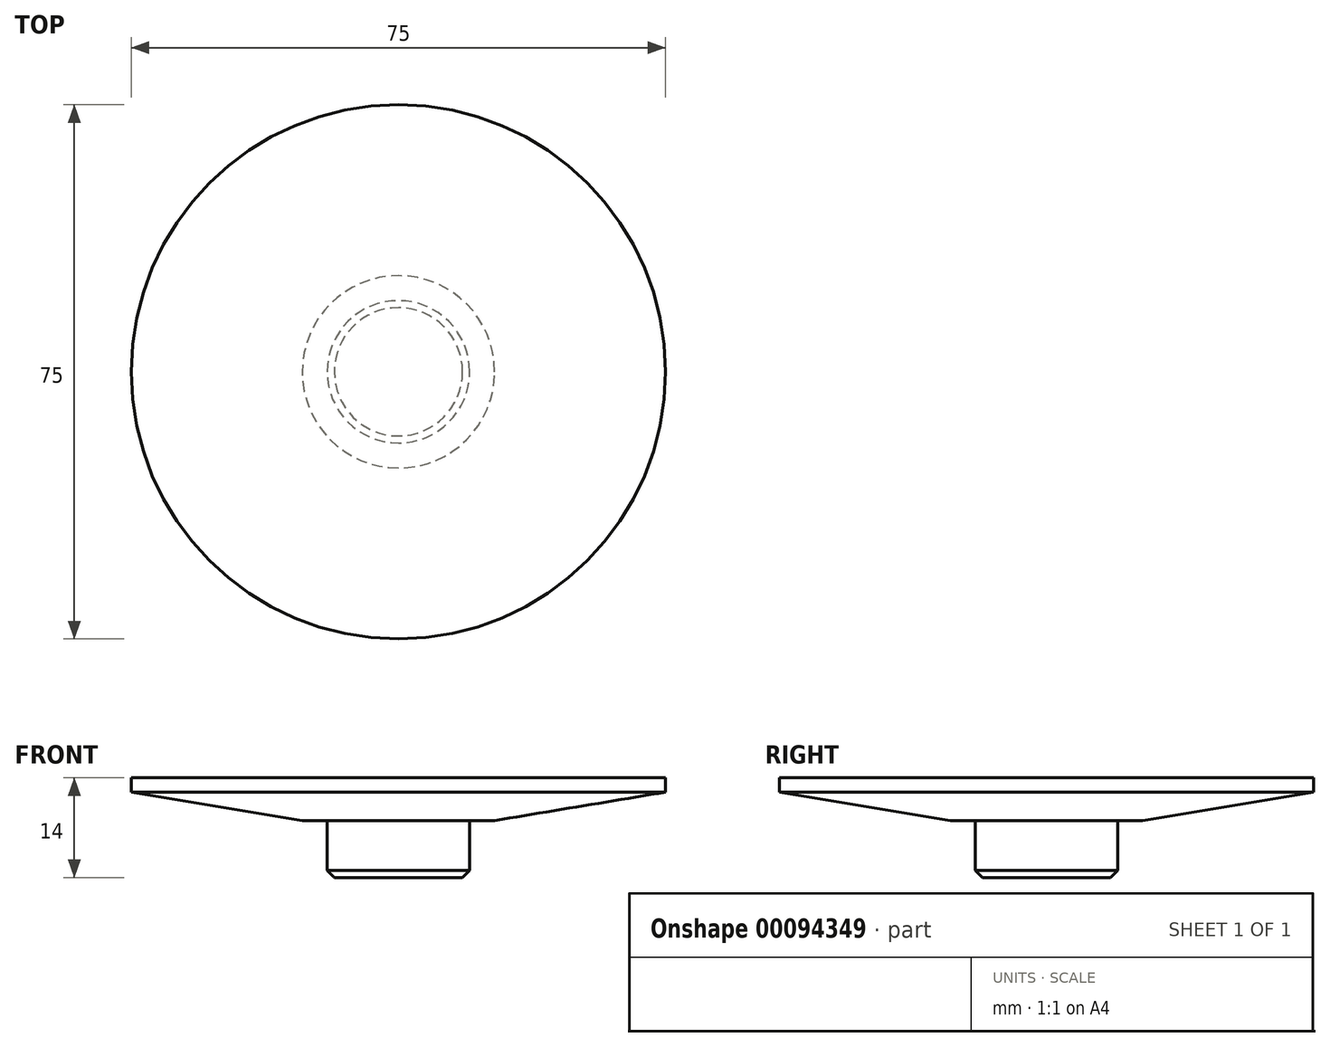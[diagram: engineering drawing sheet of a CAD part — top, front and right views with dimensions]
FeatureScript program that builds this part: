
annotation { "Feature Type Name" : "Feature", "Feature Type Description" : "" }
export const myFeature = defineFeature(function(context is Context, id is Id, definition is map)
    precondition{}
    {
        {
            var Q0;
            Q0=qCreatedBy(makeId("Top.planeOp"),FACE);
            var sketch = newSketch(context, id + "F0", { "sketchPlane" : qUnion([Q0])});
            skCircle(sketch, "E0", {"center": v(0, 0) * mm, "radius": 37.5 * mm});
            skSolve(sketch);
        }
        {
            var Q0;
            Q0=makeQuery(id+"F0.imprint","IMPRINT",FACE,{"disambiguationData":[TD([[makeQuery(id+"F0.imprint","IMPRINT",EDGE,{"derivedFrom":sQuery(id+"F0.wireOp",EDGE,"E0")}),1.0]])]});
            extrude(context, id + "F1", {"entities" : qUnion([Q0]), "depth" : 6 * mm});
        }
        {
            var Q0;
            Q0=makeQuery(id+"F1.opExtrude","CAP_EDGE",EDGE,{"disambiguationData":[OSD([sQuery(id+"F0.wireOp",EDGE,"E0")])],"isStart":true});
            chamfer(context, id + "F2", {"entities" : qUnion([Q0]), "chamferType" : ChamferType.TWO_OFFSETS, "width1" : 4 * mm, "oppositeDirection" : false, "width2" : 24 * mm, "tangentPropagation" : true});
        }
        {
            var Q0;
            Q0=makeQuery(id+"F1.opExtrude","CAP_FACE",FACE,{"disambiguationData":[OSD([sQuery(id+"F0.wireOp",EDGE,"E0")])],"isStart":true});
            var sketch = newSketch(context, id + "F3", { "sketchPlane" : qUnion([Q0])});
            skCircle(sketch, "E1", {"center": v(0, 0) * mm, "radius": 10 * mm});
            skSolve(sketch);
        }
        {
            var Q0;
            Q0=makeQuery(id+"F3.imprint","IMPRINT",FACE,{"disambiguationData":[TD([[makeQuery(id+"F3.imprint","IMPRINT",EDGE,{"derivedFrom":sQuery(id+"F3.wireOp",EDGE,"E1")}),1.0]])]});
            extrude(context, id + "F4", {"entities" : qUnion([Q0]), "operationType" : NewBodyOperationType.ADD, "depth" : 8 * mm});
        }
        {
            var Q0;
            Q0=makeQuery(id+"F4.opExtrude","CAP_EDGE",EDGE,{"disambiguationData":[OSD([sQuery(id+"F3.wireOp",EDGE,"E1")])],"isStart":false});
            chamfer(context, id + "F5", {"entities" : qUnion([Q0]), "width" : 1 * mm, "tangentPropagation" : true});
        }
    });
